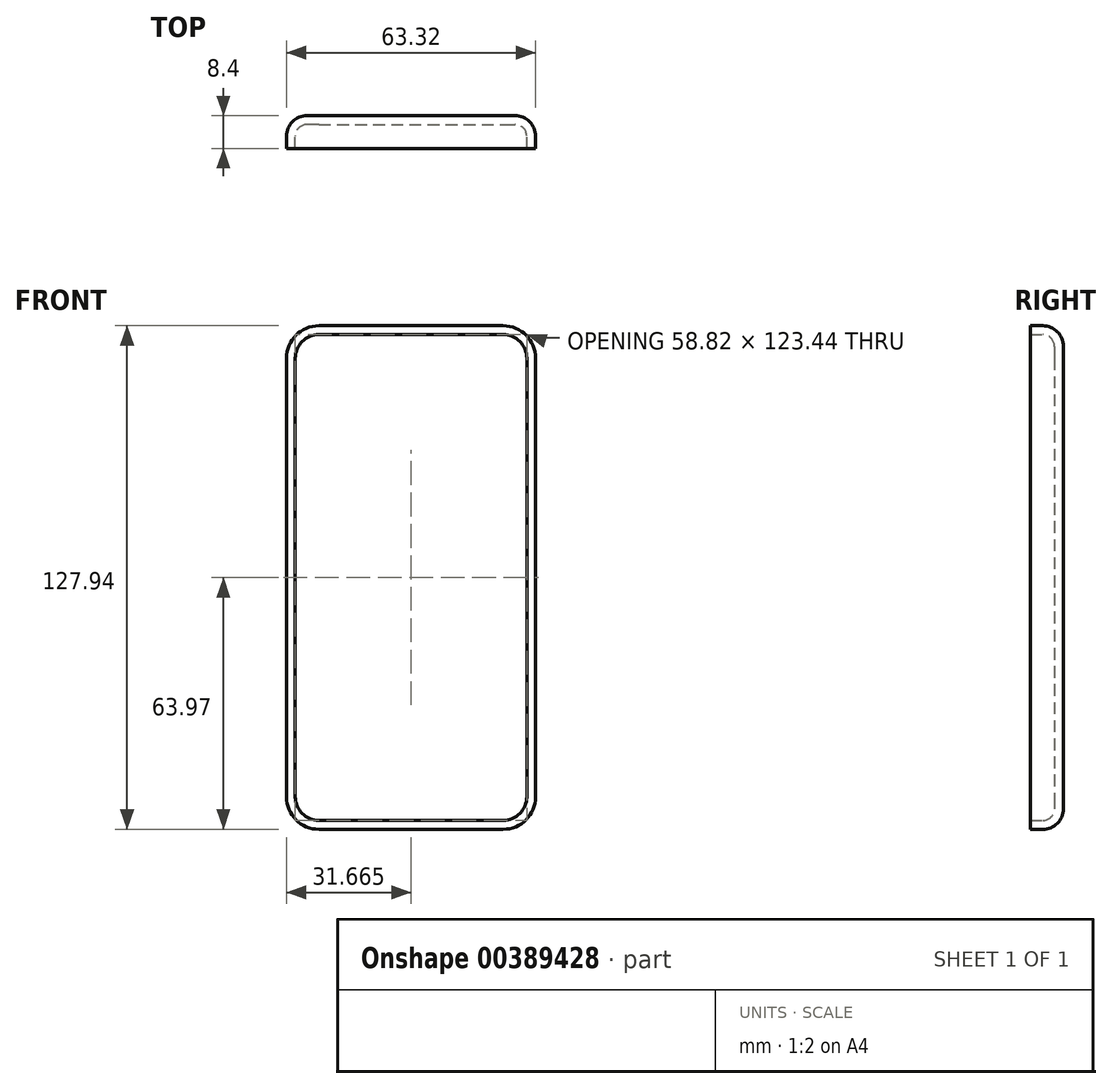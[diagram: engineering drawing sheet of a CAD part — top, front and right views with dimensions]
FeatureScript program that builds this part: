
annotation { "Feature Type Name" : "Feature", "Feature Type Description" : "" }
export const myFeature = defineFeature(function(context is Context, id is Id, definition is map)
    precondition{}
    {
        {
            var Q0;
            Q0=qCreatedBy(makeId("Front.planeOp"),FACE);
            var sketch = newSketch(context, id + "F0", { "sketchPlane" : qUnion([Q0])});
            skLineSegment(sketch, "E0", {"start": v(-47.98, 61.91) * mm, "end": v(-47.98, -49.53) * mm});
            skLineSegment(sketch, "E1", {"start": v(-41.98, 67.91) * mm, "end": v(4.84, 67.91) * mm});
            skLineSegment(sketch, "E2", {"start": v(-41.98, -55.53) * mm, "end": v(4.84, -55.53) * mm});
            skLineSegment(sketch, "E3", {"start": v(10.84, 61.91) * mm, "end": v(10.84, -49.53) * mm});
            skPoint(sketch, "E4.visualSharp", {"position": v(-47.98, 67.91) * mm});
            skArc(sketch, "E4.filletArc", {"start": v(-41.98, 67.91) * mm, "mid": v(-46.22, 66.15) * mm, "end": v(-47.98, 61.91) * mm});
            skPoint(sketch, "E5.visualSharp", {"position": v(10.84, 67.91) * mm});
            skArc(sketch, "E5.filletArc", {"start": v(10.84, 61.91) * mm, "mid": v(9.09, 66.15) * mm, "end": v(4.84, 67.91) * mm});
            skPoint(sketch, "E6.visualSharp", {"position": v(10.84, -55.53) * mm});
            skArc(sketch, "E6.filletArc", {"start": v(4.84, -55.53) * mm, "mid": v(9.09, -53.77) * mm, "end": v(10.84, -49.53) * mm});
            skPoint(sketch, "E7.visualSharp", {"position": v(-47.98, -55.53) * mm});
            skArc(sketch, "E7.filletArc", {"start": v(-47.98, -49.53) * mm, "mid": v(-46.22, -53.77) * mm, "end": v(-41.98, -55.53) * mm});
            skSolve(sketch);
        }
        {
            var Q0;
            Q0=makeQuery(id+"F0.imprint","IMPRINT",FACE,{"disambiguationData":[TD([[makeQuery(id+"F0.imprint","IMPRINT",EDGE,{"derivedFrom":sQuery(id+"F0.wireOp",EDGE,"E0")}),1.0]])]});
            extrude(context, id + "F1", {"entities" : qUnion([Q0]), "depth" : 6.15 * mm});
        }
        {
            var Q0;
            Q0=makeQuery(id+"F1.opExtrude","CAP_EDGE",EDGE,{"disambiguationData":[OSD([sQuery(id+"F0.wireOp",EDGE,"E3")])],"isStart":true});
            fillet(context, id + "F2", {"entities" : qUnion([Q0]), "radius" : 3 * mm, "tangentPropagation" : true, "allowEdgeOverflow" : false});
        }
        {
            var Q0;
            Q0=makeQuery(id+"F1.opExtrude","CAP_FACE",FACE,{"disambiguationData":[OSD([sQuery(id+"F0.wireOp",EDGE,"E0"),sQuery(id+"F0.wireOp",EDGE,"E1"),sQuery(id+"F0.wireOp",EDGE,"E2"),sQuery(id+"F0.wireOp",EDGE,"E3"),sQuery(id+"F0.wireOp",EDGE,"E4.filletArc"),sQuery(id+"F0.wireOp",EDGE,"E5.filletArc"),sQuery(id+"F0.wireOp",EDGE,"E6.filletArc"),sQuery(id+"F0.wireOp",EDGE,"E7.filletArc")])],"isStart":false});
            shell(context, id + "F3", {"entities" : qUnion([Q0]), "thickness" : 2.25 * mm, "oppositeDirection" : true});
        }
    });
